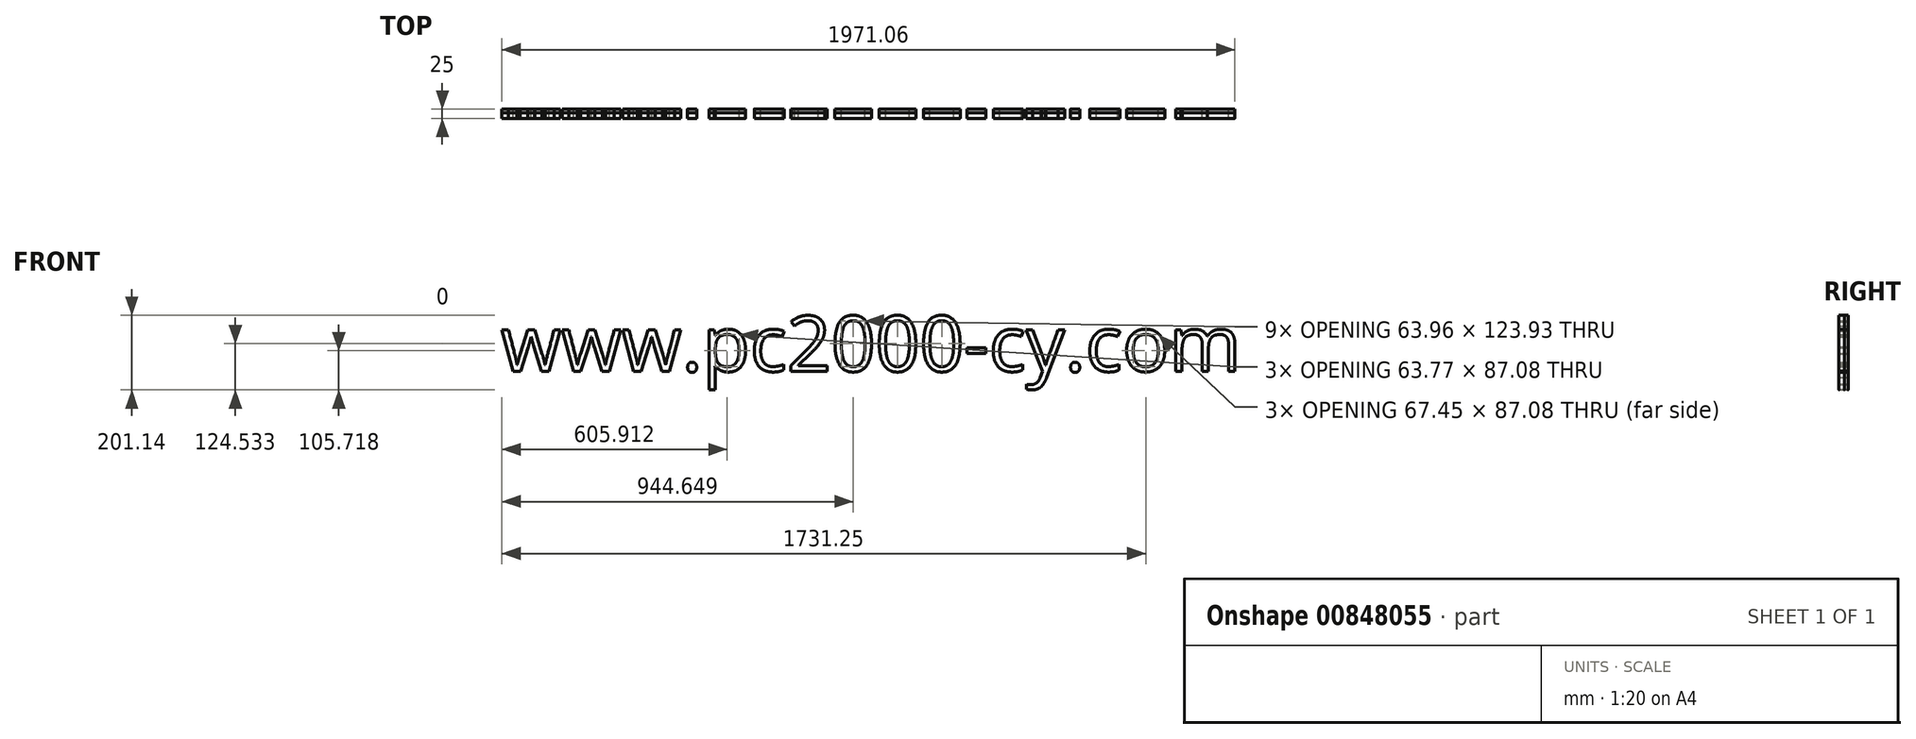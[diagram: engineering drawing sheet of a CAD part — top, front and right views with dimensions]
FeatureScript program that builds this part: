
annotation { "Feature Type Name" : "Feature", "Feature Type Description" : "" }
export const myFeature = defineFeature(function(context is Context, id is Id, definition is map)
    precondition{}
    {
        {
            var Q0;
            Q0=qCreatedBy(makeId("Front.planeOp"),FACE);
            var sketch = newSketch(context, id + "F0", { "sketchPlane" : qUnion([Q0])});
            skText(sketch, "E0", { "text": "www.pc2000-cy.com\n\n", "fontName": "OpenSans-Regular.ttf"});
            const initialGuessF0  = {"E0": [-0.35202, 0.01344, 1, 0, 0.15]};
            skSetInitialGuess(sketch, initialGuessF0);
            skSolve(sketch);
        }
        {
            var Q0;
            Q0 = qSketchRegion(id + "F0", true);
            extrude(context, id + "F1", {"entities" : qUnion([Q0]), "depth" : 10 * mm, "offsetDistance" : 25 * mm});
        }
        {
            var Q0;
            Q0 = qSketchRegion(id + "F0", true);
            extrude(context, id + "F2", {"entities" : qUnion([Q0]), "depth" : 25 * mm, "offsetDistance" : 25 * mm});
        }
        {
            var Q0;
            Q0 = qSketchRegion(id + "F0", true);
            extrude(context, id + "F3", {"entities" : qUnion([Q0]), "depth" : 25 * mm, "offsetDistance" : 25 * mm});
        }
    });
